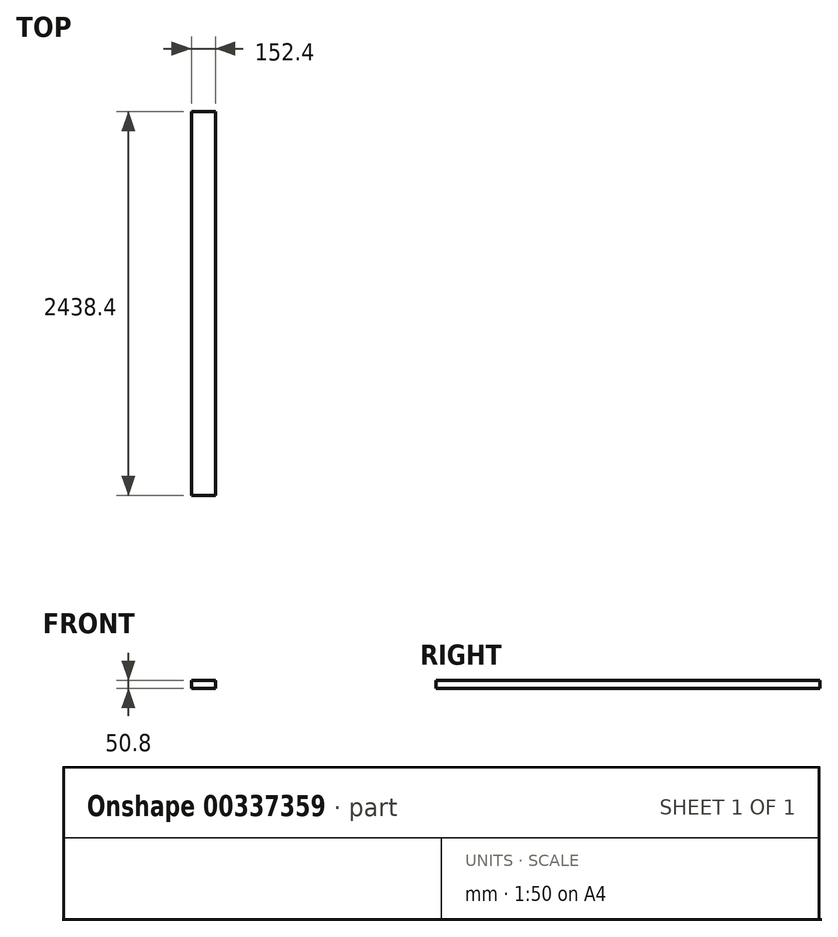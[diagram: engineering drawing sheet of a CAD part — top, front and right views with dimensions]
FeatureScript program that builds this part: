
annotation { "Feature Type Name" : "Feature", "Feature Type Description" : "" }
export const myFeature = defineFeature(function(context is Context, id is Id, definition is map)
    precondition{}
    {
        {
            var Q0;
            Q0=qCreatedBy(makeId("Front.planeOp"),FACE);
            var sketch = newSketch(context, id + "F0", { "sketchPlane" : qUnion([Q0])});
            skLineSegment(sketch, "E0.bottom", {"start": v(-107.04, 38.79) * mm, "end": v(45.36, 38.79) * mm});
            skLineSegment(sketch, "E0.top", {"start": v(-107.04, -12.01) * mm, "end": v(45.36, -12.01) * mm});
            skLineSegment(sketch, "E0.left", {"start": v(-107.04, 38.79) * mm, "end": v(-107.04, -12.01) * mm});
            skLineSegment(sketch, "E0.right", {"start": v(45.36, 38.79) * mm, "end": v(45.36, -12.01) * mm});
            skSolve(sketch);
        }
        {
            var Q0;
            Q0 = qSketchRegion(id + "F0", true);
            extrude(context, id + "F1", {"entities" : qUnion([Q0]), "depth" : 2438.4 * mm});
        }
    });
